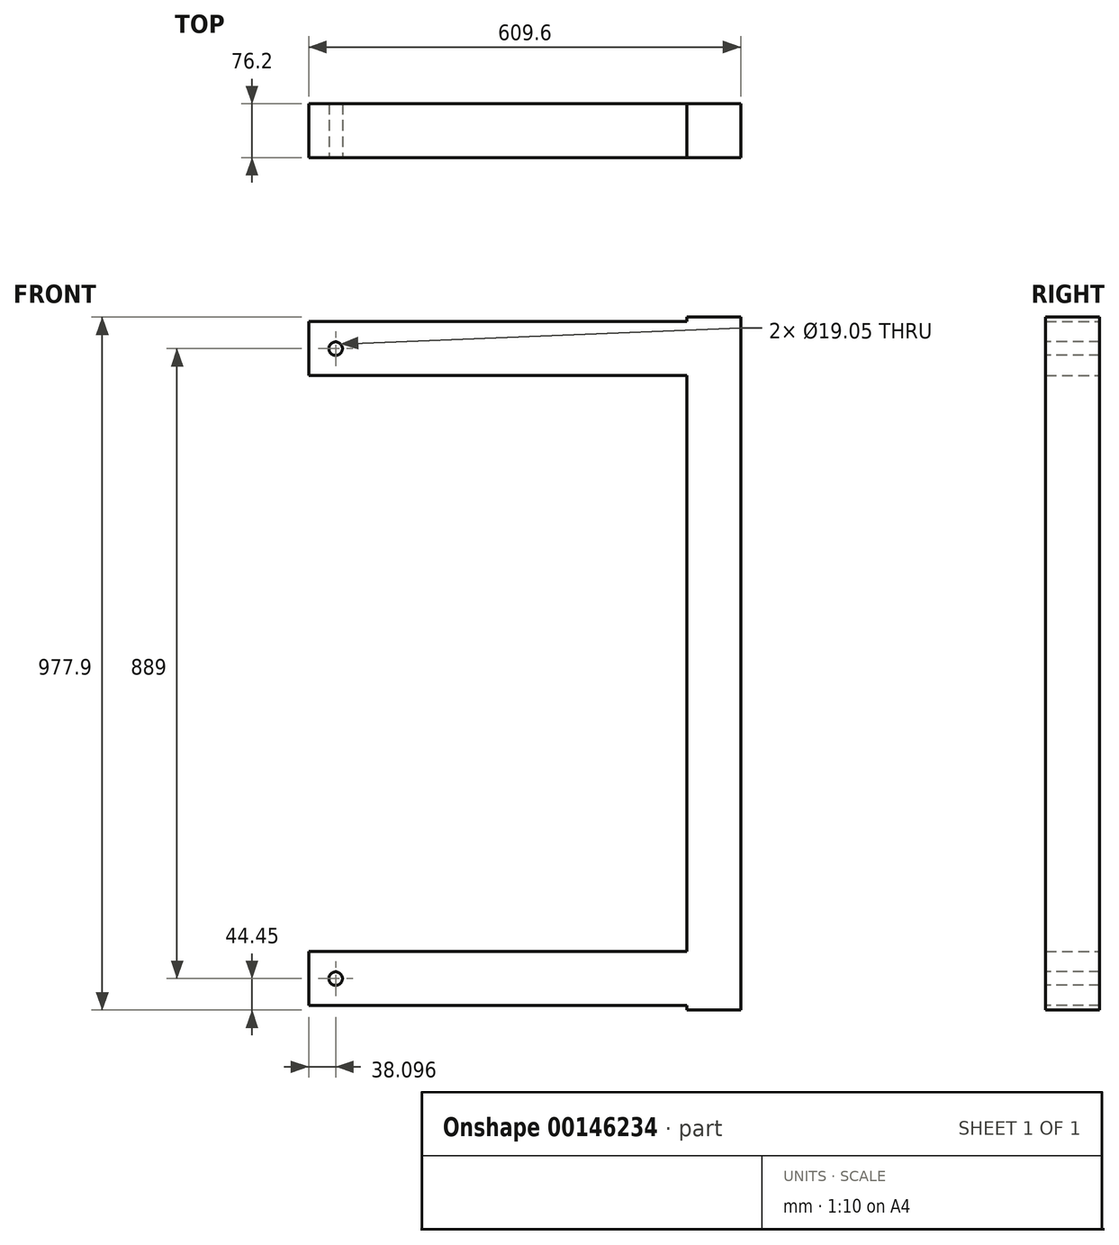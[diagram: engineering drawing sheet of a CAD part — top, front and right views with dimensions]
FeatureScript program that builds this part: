
annotation { "Feature Type Name" : "Feature", "Feature Type Description" : "" }
export const myFeature = defineFeature(function(context is Context, id is Id, definition is map)
    precondition{}
    {
        {
            var Q0;
            Q0=qCreatedBy(makeId("Top.planeOp"),FACE);
            var sketch = newSketch(context, id + "F0", { "sketchPlane" : qUnion([Q0])});
            skLineSegment(sketch, "E0.bottom", {"start": v(-224.13, 41.12) * mm, "end": v(233.07, 41.12) * mm});
            skLineSegment(sketch, "E0.top", {"start": v(-224.13, -35.08) * mm, "end": v(233.07, -35.08) * mm});
            skLineSegment(sketch, "E0.left", {"start": v(-224.13, 41.12) * mm, "end": v(-224.13, -35.08) * mm});
            skLineSegment(sketch, "E0.right", {"start": v(233.07, 41.12) * mm, "end": v(233.07, -35.08) * mm});
            skSolve(sketch);
        }
        {
            var Q0;
            Q0=makeQuery(id+"F0.imprint","IMPRINT",FACE,{"disambiguationData":[TD([[makeQuery(id+"F0.imprint","IMPRINT",EDGE,{"derivedFrom":sQuery(id+"F0.wireOp",EDGE,"E0.bottom")}),-1.0]])]});
            extrude(context, id + "F1", {"entities" : qUnion([Q0]), "depth" : 76.2 * mm});
        }
        {
            var Q0;
            Q0=makeQuery(id+"F1.opExtrude","SWEPT_FACE",FACE,{"disambiguationData":[OSD([sQuery(id+"F0.wireOp",EDGE,"E0.right")])]});
            extrude(context, id + "F2", {"entities" : qUnion([Q0]), "operationType" : NewBodyOperationType.ADD, "depth" : 152.4 * mm});
        }
        {
            var Q0;
            {var subQ0=sQuery(id+"F0.wireOp",EDGE,"E0.right");Q0=makeQuery(id+"F2.boolean.opBoolean","MERGE",FACE,{"derivedFrom":[makeQuery(id+"F1.opExtrude","CAP_FACE",FACE,{"disambiguationData":[OSD([sQuery(id+"F0.wireOp",EDGE,"E0.bottom"),sQuery(id+"F0.wireOp",EDGE,"E0.top"),sQuery(id+"F0.wireOp",EDGE,"E0.left"),subQ0])],"isStart":false}),makeQuery(id+"F2.opExtrude","SWEPT_FACE",FACE,{"disambiguationData":[OSD([subQ0]),TDD([makeQuery(id+"F1.opExtrude","CAP_EDGE",EDGE,{"disambiguationData":[OSD([subQ0])],"isStart":false})])]})]});}
            var sketch = newSketch(context, id + "F3", { "sketchPlane" : qUnion([Q0])});
            skLineSegment(sketch, "E1.bottom", {"start": v(385.47, -35.08) * mm, "end": v(309.27, -35.08) * mm});
            skLineSegment(sketch, "E1.top", {"start": v(385.47, 41.12) * mm, "end": v(309.27, 41.12) * mm});
            skLineSegment(sketch, "E1.left", {"start": v(385.47, -35.08) * mm, "end": v(385.47, 41.12) * mm});
            skLineSegment(sketch, "E1.right", {"start": v(309.27, -35.08) * mm, "end": v(309.27, 41.12) * mm});
            skSolve(sketch);
        }
        {
            var Q0;
            Q0=makeQuery(id+"F3.imprint","IMPRINT",FACE,{"disambiguationData":[TD([[makeQuery(id+"F3.imprint","IMPRINT",EDGE,{"derivedFrom":sQuery(id+"F3.wireOp",EDGE,"E1.bottom")}),1.0]])]});
            extrude(context, id + "F4", {"entities" : qUnion([Q0]), "operationType" : NewBodyOperationType.ADD, "depth" : 895.35 * mm});
        }
        {
            var Q0;
            {var subQ0=sQuery(id+"F0.wireOp",EDGE,"E0.right");Q0=makeQuery(id+"F2.boolean.opBoolean","MERGE",FACE,{"derivedFrom":[makeQuery(id+"F1.opExtrude","CAP_FACE",FACE,{"disambiguationData":[OSD([sQuery(id+"F0.wireOp",EDGE,"E0.bottom"),sQuery(id+"F0.wireOp",EDGE,"E0.top"),sQuery(id+"F0.wireOp",EDGE,"E0.left"),subQ0])],"isStart":true}),makeQuery(id+"F2.opExtrude","SWEPT_FACE",FACE,{"disambiguationData":[OSD([subQ0]),TDD([makeQuery(id+"F1.opExtrude","CAP_EDGE",EDGE,{"disambiguationData":[OSD([subQ0])],"isStart":true})])]})]});}
            var sketch = newSketch(context, id + "F5", { "sketchPlane" : qUnion([Q0])});
            skLineSegment(sketch, "E2.bottom", {"start": v(385.47, -41.12) * mm, "end": v(309.27, -41.12) * mm});
            skLineSegment(sketch, "E2.top", {"start": v(385.47, 35.08) * mm, "end": v(309.27, 35.08) * mm});
            skLineSegment(sketch, "E2.left", {"start": v(385.47, -41.12) * mm, "end": v(385.47, 35.08) * mm});
            skLineSegment(sketch, "E2.right", {"start": v(309.27, -41.12) * mm, "end": v(309.27, 35.08) * mm});
            skSolve(sketch);
        }
        {
            var Q0;
            Q0=makeQuery(id+"F5.imprint","IMPRINT",FACE,{"disambiguationData":[TD([[makeQuery(id+"F5.imprint","IMPRINT",EDGE,{"derivedFrom":sQuery(id+"F5.wireOp",EDGE,"E2.bottom")}),1.0]])]});
            extrude(context, id + "F12", {"entities" : qUnion([Q0]), "operationType" : NewBodyOperationType.ADD, "depth" : 6.35 * mm});
        }
        {
            var Q0;
            Q0=makeQuery(id+"F4.opExtrude","SWEPT_FACE",FACE,{"disambiguationData":[OSD([sQuery(id+"F3.wireOp",EDGE,"E1.right")])]});
            var sketch = newSketch(context, id + "F6", { "sketchPlane" : qUnion([Q0])});
            skLineSegment(sketch, "E3.bottom", {"start": v(35.08, 965.2) * mm, "end": v(-41.12, 965.2) * mm});
            skLineSegment(sketch, "E3.top", {"start": v(35.08, 889) * mm, "end": v(-41.12, 889) * mm});
            skLineSegment(sketch, "E3.left", {"start": v(35.08, 965.2) * mm, "end": v(35.08, 889) * mm});
            skLineSegment(sketch, "E3.right", {"start": v(-41.12, 965.2) * mm, "end": v(-41.12, 889) * mm});
            skSolve(sketch);
        }
        {
            var Q0;
            Q0=makeQuery(id+"F6.imprint","IMPRINT",FACE,{"disambiguationData":[TD([[makeQuery(id+"F6.imprint","IMPRINT",EDGE,{"derivedFrom":sQuery(id+"F6.wireOp",EDGE,"E3.bottom")}),1.0]])]});
            extrude(context, id + "F7", {"entities" : qUnion([Q0]), "operationType" : NewBodyOperationType.ADD, "depth" : 533.4 * mm});
        }
        {
            var Q0;
            {var subQ0=sQuery(id+"F0.wireOp",EDGE,"E0.top");Q0=makeQuery(id+"F7.boolean.opBoolean","MERGE",FACE,{"derivedFrom":[makeQuery(id+"F12.boolean.opBoolean","MERGE",FACE,{"derivedFrom":[makeQuery(id+"F4.boolean.opBoolean","MERGE",FACE,{"derivedFrom":[makeQuery(id+"F2.boolean.opBoolean","MERGE",FACE,{"derivedFrom":[makeQuery(id+"F1.opExtrude","SWEPT_FACE",FACE,{"disambiguationData":[OSD([subQ0])]}),makeQuery(id+"F2.opExtrude","SWEPT_FACE",FACE,{"disambiguationData":[OSD([subQ0,sQuery(id+"F0.wireOp",EDGE,"E0.right")])]})]}),makeQuery(id+"F4.opExtrude","SWEPT_FACE",FACE,{"disambiguationData":[OSD([sQuery(id+"F3.wireOp",EDGE,"E1.bottom")])]})]}),makeQuery(id+"F12.opExtrude","SWEPT_FACE",FACE,{"disambiguationData":[OSD([sQuery(id+"F5.wireOp",EDGE,"E2.top")])]})]}),makeQuery(id+"F7.opExtrude","SWEPT_FACE",FACE,{"disambiguationData":[OSD([sQuery(id+"F6.wireOp",EDGE,"E3.left")])]})]});}
            var sketch = newSketch(context, id + "F8", { "sketchPlane" : qUnion([Q0])});
            skCircle(sketch, "E4", {"center": v(-186.03, 927.1) * mm, "radius": 9.53 * mm});
            skPoint(sketch, "E4.centerSnap0", {"position": v(-224.13, 927.1) * mm});
            skLineSegment(sketch, "E5", {"start": v(-186.03, 927.1) * mm, "end": v(-224.13, 927.1) * mm});
            skSolve(sketch);
        }
        {
            var Q0;
            Q0=makeQuery(id+"F8.imprint","IMPRINT",FACE,{"disambiguationData":[TD([[makeQuery(id+"F8.imprint","IMPRINT",EDGE,{"derivedFrom":sQuery(id+"F8.wireOp",EDGE,"E4")}),1.0]])]});
            extrude(context, id + "F9", {"entities" : qUnion([Q0]), "operationType" : NewBodyOperationType.REMOVE, "oppositeDirection" : true, "depth" : 76.2 * mm});
        }
        {
            var Q0;
            {var subQ0=sQuery(id+"F0.wireOp",EDGE,"E0.top");Q0=makeQuery(id+"F7.boolean.opBoolean","MERGE",FACE,{"derivedFrom":[makeQuery(id+"F12.boolean.opBoolean","MERGE",FACE,{"derivedFrom":[makeQuery(id+"F4.boolean.opBoolean","MERGE",FACE,{"derivedFrom":[makeQuery(id+"F2.boolean.opBoolean","MERGE",FACE,{"derivedFrom":[makeQuery(id+"F1.opExtrude","SWEPT_FACE",FACE,{"disambiguationData":[OSD([subQ0])]}),makeQuery(id+"F2.opExtrude","SWEPT_FACE",FACE,{"disambiguationData":[OSD([subQ0,sQuery(id+"F0.wireOp",EDGE,"E0.right")])]})]}),makeQuery(id+"F4.opExtrude","SWEPT_FACE",FACE,{"disambiguationData":[OSD([sQuery(id+"F3.wireOp",EDGE,"E1.bottom")])]})]}),makeQuery(id+"F12.opExtrude","SWEPT_FACE",FACE,{"disambiguationData":[OSD([sQuery(id+"F5.wireOp",EDGE,"E2.top")])]})]}),makeQuery(id+"F7.opExtrude","SWEPT_FACE",FACE,{"disambiguationData":[OSD([sQuery(id+"F6.wireOp",EDGE,"E3.left")])]})]});}
            var sketch = newSketch(context, id + "F10", { "sketchPlane" : qUnion([Q0])});
            skLineSegment(sketch, "E6", {"start": v(-224.13, 38.1) * mm, "end": v(-186.03, 38.1) * mm});
            skCircle(sketch, "E7", {"center": v(-186.03, 38.1) * mm, "radius": 9.53 * mm});
            skSolve(sketch);
        }
        {
            var Q0;
            Q0=makeQuery(id+"F10.imprint","IMPRINT",FACE,{"disambiguationData":[TD([[makeQuery(id+"F10.imprint","IMPRINT",EDGE,{"derivedFrom":sQuery(id+"F10.wireOp",EDGE,"E7")}),1.0]])]});
            extrude(context, id + "F11", {"entities" : qUnion([Q0]), "operationType" : NewBodyOperationType.REMOVE, "oppositeDirection" : true, "depth" : 76.2 * mm});
        }
    });
